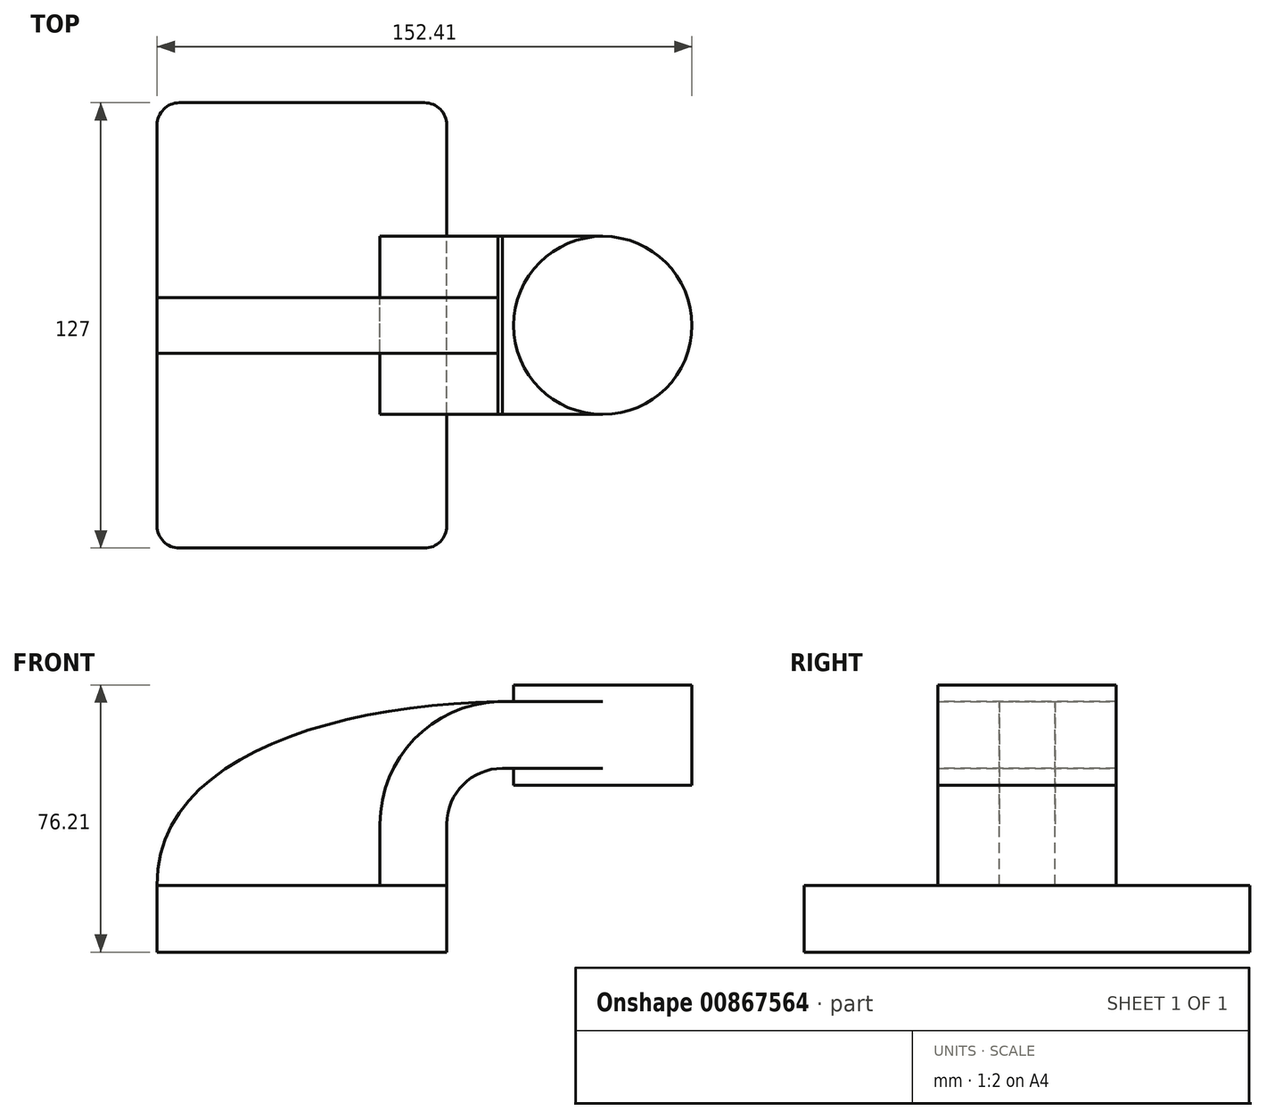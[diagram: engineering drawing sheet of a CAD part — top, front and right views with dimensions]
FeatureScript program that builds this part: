
annotation { "Feature Type Name" : "Feature", "Feature Type Description" : "" }
export const myFeature = defineFeature(function(context is Context, id is Id, definition is map)
    precondition{}
    {
        {
            var Q0;
            Q0=qCreatedBy(makeId("Front.planeOp"),FACE);
            var sketch = newSketch(context, id + "F0", { "sketchPlane" : qUnion([Q0])});
            skLineSegment(sketch, "E0.bottom", {"start": v(-41.28, -9.53) * mm, "end": v(41.28, -9.53) * mm});
            skLineSegment(sketch, "E0.top", {"start": v(-41.28, 9.53) * mm, "end": v(41.28, 9.53) * mm});
            skLineSegment(sketch, "E0.left", {"start": v(-41.28, -9.53) * mm, "end": v(-41.28, 9.53) * mm});
            skLineSegment(sketch, "E0.right", {"start": v(41.28, -9.53) * mm, "end": v(41.28, 9.53) * mm});
            skPoint(sketch, "E0.middle", {"position": v(0, 0) * mm});
            skLineSegment(sketch, "E1.bottom", {"start": v(60.33, 38.1) * mm, "end": v(111.12, 38.1) * mm});
            skLineSegment(sketch, "E1.top", {"start": v(60.33, 66.67) * mm, "end": v(111.12, 66.67) * mm});
            skLineSegment(sketch, "E1.left", {"start": v(60.33, 38.1) * mm, "end": v(60.33, 66.67) * mm});
            skLineSegment(sketch, "E1.right", {"start": v(111.12, 38.1) * mm, "end": v(111.12, 66.67) * mm});
            skPoint(sketch, "E1.middle", {"position": v(85.72, 52.39) * mm});
            skLineSegment(sketch, "E2", {"start": v(41.27, 9.53) * mm, "end": v(41.27, 27) * mm});
            skArc(sketch, "E3", {"start": v(41.27, 27) * mm, "mid": v(45.92, 38.23) * mm, "end": v(57.15, 42.88) * mm});
            skLineSegment(sketch, "E4", {"start": v(57.15, 42.88) * mm, "end": v(85.72, 42.88) * mm});
            skPoint(sketch, "E4.endSnap0", {"position": v(85.72, 38.1) * mm});
            skLineSegment(sketch, "E5.0", {"start": v(57.15, 61.93) * mm, "end": v(85.72, 61.93) * mm});
            skArc(sketch, "E5.1", {"start": v(22.23, 27) * mm, "mid": v(32.45, 51.7) * mm, "end": v(57.15, 61.93) * mm});
            skLineSegment(sketch, "E5.2", {"start": v(22.22, 9.53) * mm, "end": v(22.22, 27) * mm});
            skLineSegment(sketch, "E6", {"start": v(85.72, 66.67) * mm, "end": v(85.72, 38.1) * mm});
            skFitSpline(sketch, "E7", {"points": [v(-41.28, 9.53) * mm, v(57.15, 61.93) * mm], "startDerivative": vector(-0.87, 109.22) * mm, "endDerivative": vector(145.83, 2.43) * mm});
            skLineSegment(sketch, "E8", {"start": v(22.22, 9.52) * mm, "end": v(41.28, 9.52) * mm});
            skSolve(sketch);
        }
        {
            var Q0;
            Q0=makeQuery(id+"F0.imprint","IMPRINT",FACE,{"disambiguationData":[TD([[makeQuery(id+"F0.imprint","IMPRINT",EDGE,{"derivedFrom":sQuery(id+"F0.wireOp",EDGE,"E0.bottom")}),1.0]])]});
            extrude(context, id + "F1", {"entities" : qUnion([Q0]), "endBound" : BoundingType.SYMMETRIC, "depth" : 127 * mm, "offsetDistance" : 25.4 * mm});
        }
        {
            var Q0;
            Q0=makeQuery(id+"F0.imprint","IMPRINT",FACE,{"disambiguationData":[TD([[makeQuery(id+"F0.imprint","IMPRINT",EDGE,{"derivedFrom":sQuery(id+"F0.wireOp",EDGE,"E2")}),1.0]])]});
            var Q1;
            {var subQ0=sQuery(id+"F0.wireOp",EDGE,"E4");var subQ1=sQuery(id+"F0.wireOp",EDGE,"E1.left");var subQ2=makeQuery(id+"F0.imprint","INTERSECT",VERTEX,{"derivedFrom":[subQ1,subQ0]});Q1=makeQuery(id+"F0.imprint","IMPRINT",FACE,{"disambiguationData":[TD([[makeQuery(id+"F0.imprint","IMPRINT",EDGE,{"disambiguationData":[TD([[subQ2,-1.0]])],"derivedFrom":subQ1}),-1.0]])]});}
            extrude(context, id + "F2", {"entities" : qUnion([Q0, Q1]), "endBound" : BoundingType.SYMMETRIC, "depth" : 50.8 * mm, "offsetDistance" : 25.4 * mm});
        }
        {
            var Q0;
            {var subQ0=sQuery(id+"F0.wireOp",EDGE,"E0.top");Q0=makeQuery(id+"F0.imprint","IMPRINT",FACE,{"disambiguationData":[TD([[makeQuery(id+"F0.imprint","IMPRINT",EDGE,{"derivedFrom":subQ0}),1.0]])]});}
            extrude(context, id + "F3", {"entities" : qUnion([Q0]), "endBound" : BoundingType.SYMMETRIC, "depth" : 15.88 * mm, "offsetDistance" : 25.4 * mm});
        }
        {
            var Q0;
            {var subQ4=sQuery(id+"F0.wireOp",EDGE,"E1.right");Q0=makeQuery(id+"F0.imprint","IMPRINT",FACE,{"disambiguationData":[TD([[makeQuery(id+"F0.imprint","IMPRINT",EDGE,{"derivedFrom":subQ4}),1.0]])]});}
            var Q1;
            Q1=sQuery(id+"F0.wireOp",EDGE,"E6");
            revolve(context, id + "F4", {"operationType" : NewBodyOperationType.ADD, "surfaceOperationType" : NewSurfaceOperationType.NEW, "entities" : qUnion([Q0]), "axis" : qUnion([Q1]), "revolveType" : RevolveType.FULL});
        }
        {
            var Q0;
            Q0=makeQuery(id+"F1.opExtrude","CAP_EDGE",EDGE,{"disambiguationData":[OSD([sQuery(id+"F0.wireOp",EDGE,"E0.left")])],"isStart":false});
            var Q1;
            Q1=makeQuery(id+"F1.opExtrude","CAP_EDGE",EDGE,{"disambiguationData":[OSD([sQuery(id+"F0.wireOp",EDGE,"E0.right")])],"isStart":false});
            var Q2;
            Q2=makeQuery(id+"F1.opExtrude","CAP_EDGE",EDGE,{"disambiguationData":[OSD([sQuery(id+"F0.wireOp",EDGE,"E0.left")])],"isStart":true});
            var Q3;
            Q3=makeQuery(id+"F1.opExtrude","CAP_EDGE",EDGE,{"disambiguationData":[OSD([sQuery(id+"F0.wireOp",EDGE,"E0.right")])],"isStart":true});
            fillet(context, id + "F5", {"entities" : qUnion([Q0, Q1, Q2, Q3]), "radius" : 6.35 * mm, "tangentPropagation" : true, "allowEdgeOverflow" : false});
        }
    });
